# Revit family: Haworth_Compose_Panel_Tile_Special
name_source: partatom
category: Furniture Systems
revit_build: Autodesk Revit 2018 (Build: 20170223_1515(x64)
units: mm (PartAtom-declared; Revit-internal decimal feet)

## family parameters
Always vertical = Yes
Cut with Voids When Loaded = No
OmniClass Number = 23.40.70.14.64.21
OmniClass Title = Systems Furniture
Part Type = Normal
Room Calculation Point = No
Round Connector Dimension = Use Diameter
Shared = No
Work Plane-Based = No

## types (1)
- Tackboard 36" x 84"
    Actual Height = 36"
    Actual Width = 84"
    Assembly Code = E2020500
    Custom Size = Yes
    Description = Haworth_Compose-Panel_Accessories-External_Mount_Special
    Height = 36"
    Manufacturer = Haworth
    Markerboard = No
    Markerboard Tray Finish = Haworth - Metal - Brushed Aluminum
    Max. Height = 32"
    Min. Height = 16"
    Min. Width = 24"
    Model = Haworth_Compose-Panel_Accessories-External_Mount_Special
    Panel Depth = 5/8"
    Panel Finish = Haworth - Fabric - Tellure - Sky 3A-32
    Panel Height = 36"
    Panel Width = 84"
    Revision Number = 3
    Size = Verify Final Dim. w/ Haworth
    Slat Tile = No
    Sustainability Info = http://media.haworth.com
    Tackboard = Yes
    URL = www.haworth.com
    URL - Product = https://www.haworth.com
    Warranty = http://www.haworth.com
    Width = 84"

## geometry (parser evidence)
native form markers: Blend x2, Sweep x6
no freeform markers — native parametric forms only
